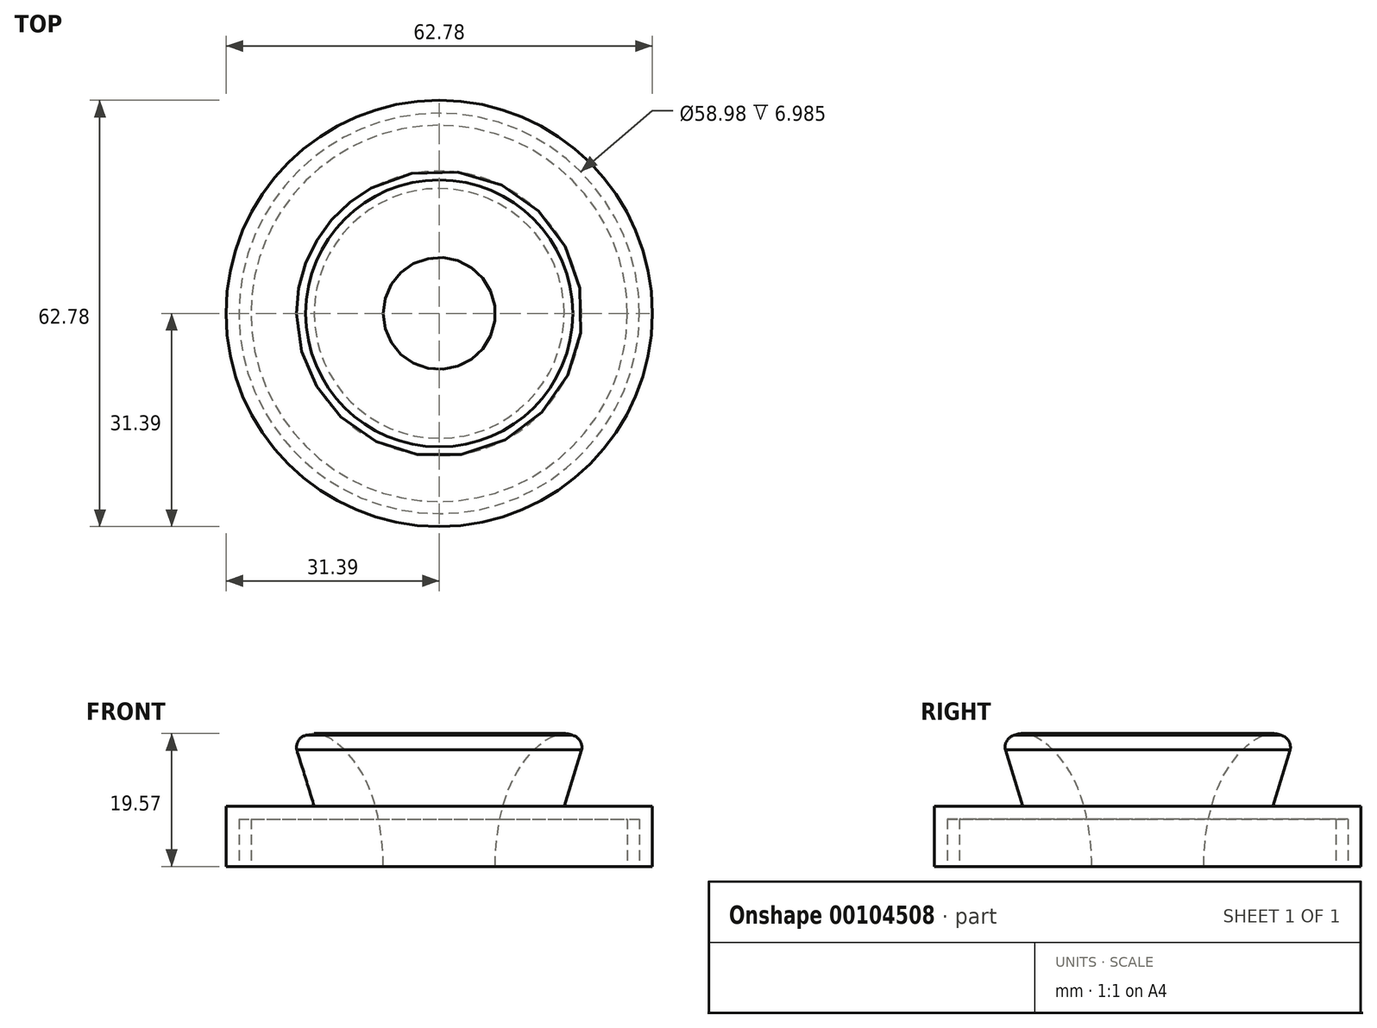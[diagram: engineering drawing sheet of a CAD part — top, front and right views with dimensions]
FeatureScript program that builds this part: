
annotation { "Feature Type Name" : "Feature", "Feature Type Description" : "" }
export const myFeature = defineFeature(function(context is Context, id is Id, definition is map)
    precondition{}
    {
        {
            var Q0;
            Q0=qCreatedBy(makeId("Front.planeOp"),FACE);
            var sketch = newSketch(context, id + "F0", { "sketchPlane" : qUnion([Q0])});
            skLineSegment(sketch, "E0", {"start": v(8.26, 0) * mm, "end": v(27.71, 0) * mm});
            skLineSegment(sketch, "E1", {"start": v(27.71, 0) * mm, "end": v(27.71, 6.99) * mm});
            skLineSegment(sketch, "E2", {"start": v(27.71, 6.99) * mm, "end": v(29.49, 6.99) * mm});
            skLineSegment(sketch, "E3", {"start": v(29.49, 6.99) * mm, "end": v(29.49, 0) * mm});
            skLineSegment(sketch, "E4", {"start": v(29.49, 0) * mm, "end": v(31.4, 0) * mm});
            skLineSegment(sketch, "E5", {"start": v(31.4, 0) * mm, "end": v(31.4, 8.9) * mm});
            skLineSegment(sketch, "E6", {"start": v(31.4, 8.9) * mm, "end": v(18.4, 8.9) * mm});
            skFitSpline(sketch, "E7", {"points": [v(8.26, 0) * mm, v(9.22, 8.19) * mm, v(13.15, 16.3) * mm, v(19.66, 19.32) * mm], "startDerivative": vector(-0.3, 20.62) * mm, "endDerivative": vector(20.8, -9.1) * mm});
            skLineSegment(sketch, "E8", {"start": v(18.4, 8.89) * mm, "end": v(20.97, 17.18) * mm});
            skLineSegment(sketch, "E9", {"start": v(0, 0) * mm, "end": v(0, 16.89) * mm, "construction": true});
            skArc(sketch, "E10", {"start": v(20.97, 17.18) * mm, "mid": v(20.74, 18.5) * mm, "end": v(19.66, 19.32) * mm});
            skSolve(sketch);
        }
        {
            var Q0;
            Q0=makeQuery(id+"F0.imprint","IMPRINT",FACE,{"disambiguationData":[TD([[makeQuery(id+"F0.imprint","IMPRINT",EDGE,{"derivedFrom":sQuery(id+"F0.wireOp",EDGE,"E0")}),1.0]])]});
            var Q1;
            Q1=sQuery(id+"F0.wireOp",EDGE,"E9");
            revolve(context, id + "F1", {"entities" : qUnion([Q0]), "axis" : qUnion([Q1]), "revolveType" : RevolveType.FULL});
        }
    });
